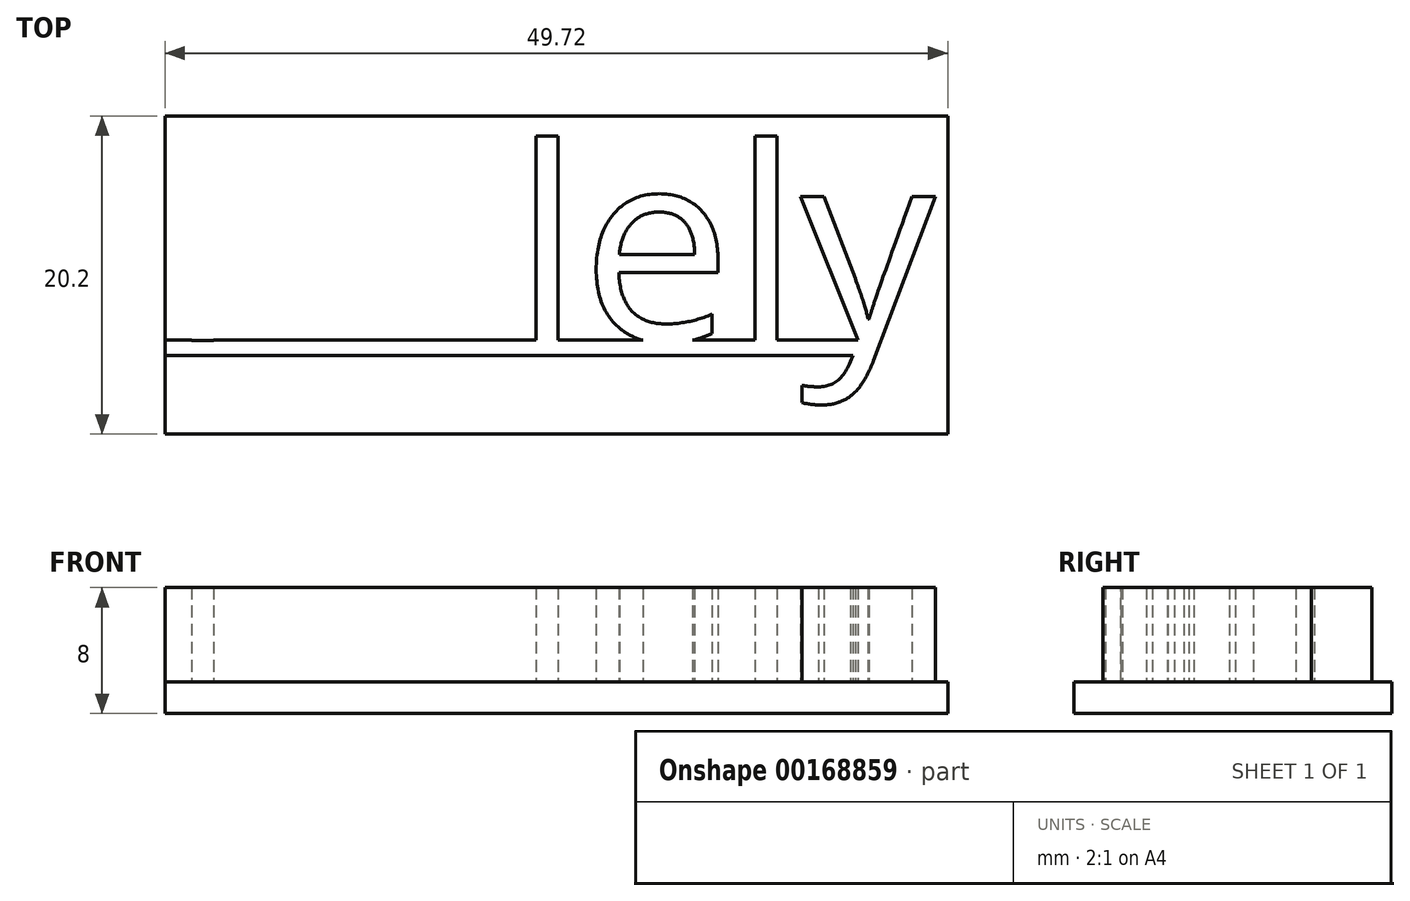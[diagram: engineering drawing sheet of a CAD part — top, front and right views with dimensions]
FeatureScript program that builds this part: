
annotation { "Feature Type Name" : "Feature", "Feature Type Description" : "" }
export const myFeature = defineFeature(function(context is Context, id is Id, definition is map)
    precondition{}
    {
        {
            var Q0;
            Q0=qCreatedBy(makeId("Top.planeOp"),FACE);
            var sketch = newSketch(context, id + "F0", { "sketchPlane" : qUnion([Q0])});
            skText(sketch, "E0", { "text": "Halely", "fontName": "OpenSans-Regular.ttf"});
            skLineSegment(sketch, "E1.bottom", {"start": v(0, -12.3) * mm, "end": v(50, -12.3) * mm});
            skLineSegment(sketch, "E1.top", {"start": v(0, -13.27) * mm, "end": v(50, -13.27) * mm});
            skLineSegment(sketch, "E1.left", {"start": v(0, -12.3) * mm, "end": v(0, -13.27) * mm});
            skLineSegment(sketch, "E1.right", {"start": v(50, -12.3) * mm, "end": v(50, -13.27) * mm});
            const initialGuessF0  = {"E0": [0, -0.0123, 1, 0, 0.0123]};
            skSetInitialGuess(sketch, initialGuessF0);
            skSolve(sketch);
        }
        {
            var Q0;
            {var subQ0=sQuery(id+"F0.wireOp",EDGE,"E0.sketch_text.stroke-1");Q0=makeQuery(id+"F0.imprint","IMPRINT",FACE,{"disambiguationData":[TD([[makeQuery(id+"F0.imprint","IMPRINT",EDGE,{"derivedFrom":subQ0}),-1.0]])]});}
            var Q1;
            {var subQ16=sQuery(id+"F0.wireOp",EDGE,"E0.sketch_text.stroke-56");Q1=makeQuery(id+"F0.imprint","IMPRINT",FACE,{"disambiguationData":[TD([[makeQuery(id+"F0.imprint","IMPRINT",EDGE,{"derivedFrom":subQ16}),1.0]])]});}
            var Q2;
            {var subQ5=sQuery(id+"F0.wireOp",EDGE,"E0.sketch_text.stroke-12");Q2=makeQuery(id+"F0.imprint","IMPRINT",FACE,{"disambiguationData":[TD([[makeQuery(id+"F0.imprint","IMPRINT",EDGE,{"derivedFrom":subQ5}),-1.0]])]});}
            var Q3;
            {var subQ0=sQuery(id+"F0.wireOp",EDGE,"E0.sketch_text.stroke-40");Q3=makeQuery(id+"F0.imprint","IMPRINT",FACE,{"disambiguationData":[TD([[makeQuery(id+"F0.imprint","IMPRINT",EDGE,{"derivedFrom":subQ0}),-1.0]])]});}
            var Q4;
            {var subQ0=sQuery(id+"F0.wireOp",EDGE,"E0.sketch_text.stroke-44");Q4=makeQuery(id+"F0.imprint","IMPRINT",FACE,{"disambiguationData":[TD([[makeQuery(id+"F0.imprint","IMPRINT",EDGE,{"derivedFrom":subQ0}),-1.0]])]});}
            var Q5;
            {var subQ0=sQuery(id+"F0.wireOp",EDGE,"E0.sketch_text.stroke-63");Q5=makeQuery(id+"F0.imprint","IMPRINT",FACE,{"disambiguationData":[TD([[makeQuery(id+"F0.imprint","IMPRINT",EDGE,{"derivedFrom":subQ0}),-1.0]])]});}
            var Q6;
            {var subQ0=sQuery(id+"F0.wireOp",EDGE,"E0.sketch_text.stroke-66");Q6=makeQuery(id+"F0.imprint","IMPRINT",FACE,{"disambiguationData":[TD([[makeQuery(id+"F0.imprint","IMPRINT",EDGE,{"derivedFrom":subQ0}),-1.0]])]});}
            var Q7;
            {var subQ0=sQuery(id+"F0.wireOp",EDGE,"E1.bottom");var subQ1=sQuery(id+"F0.wireOp",EDGE,"E0.sketch_text.stroke-73");var subQ2=makeQuery(id+"F0.imprint","INTERSECT",VERTEX,{"derivedFrom":[subQ1,subQ0]});Q7=makeQuery(id+"F0.imprint","IMPRINT",FACE,{"disambiguationData":[TD([[makeQuery(id+"F0.imprint","IMPRINT",EDGE,{"disambiguationData":[TD([[subQ2,-1.0]])],"derivedFrom":subQ1}),-1.0]])]});}
            var Q8;
            {var subQ5=sQuery(id+"F0.wireOp",EDGE,"E0.sketch_text.stroke-74");Q8=makeQuery(id+"F0.imprint","IMPRINT",FACE,{"disambiguationData":[TD([[makeQuery(id+"F0.imprint","IMPRINT",EDGE,{"derivedFrom":subQ5}),-1.0]])]});}
            var Q9;
            {var subQ0=sQuery(id+"F0.wireOp",EDGE,"E0.sketch_text.stroke-56");Q9=makeQuery(id+"F0.imprint","IMPRINT",FACE,{"disambiguationData":[TD([[makeQuery(id+"F0.imprint","IMPRINT",EDGE,{"derivedFrom":subQ0}),-1.0]])]});}
            var Q10;
            {var subQ0=sQuery(id+"F0.wireOp",EDGE,"E0.sketch_text.stroke-16");var subQ1=sQuery(id+"F0.wireOp",EDGE,"E0.sketch_text.stroke-15");var subQ2=makeQuery(id+"F0.imprint","INTERSECT",VERTEX,{"derivedFrom":[subQ1,subQ0]});Q10=makeQuery(id+"F0.imprint","IMPRINT",FACE,{"disambiguationData":[TD([[makeQuery(id+"F0.imprint","IMPRINT",EDGE,{"disambiguationData":[TD([[subQ2,1.0]])],"derivedFrom":subQ1}),-1.0]])]});}
            extrude(context, id + "F1", {"entities" : qUnion([Q0, Q1, Q2, Q3, Q4, Q5, Q6, Q7, Q8, Q9, Q10]), "depth" : 8 * mm});
        }
        {
            var Q0;
            Q0=qCreatedBy(makeId("Top.planeOp"),FACE);
            var sketch = newSketch(context, id + "F2", { "sketchPlane" : qUnion([Q0])});
            skLineSegment(sketch, "E2.bottom", {"start": v(49.72, -18.25) * mm, "end": v(0, -18.25) * mm});
            skLineSegment(sketch, "E2.top", {"start": v(49.72, 1.95) * mm, "end": v(0, 1.95) * mm});
            skLineSegment(sketch, "E2.left", {"start": v(49.72, -18.25) * mm, "end": v(49.72, 1.95) * mm});
            skLineSegment(sketch, "E2.right", {"start": v(0, -18.25) * mm, "end": v(0, 1.95) * mm});
            skSolve(sketch);
        }
        {
            var Q0;
            Q0 = qSketchRegion(id + "F2", true);
            extrude(context, id + "F3", {"entities" : qUnion([Q0]), "operationType" : NewBodyOperationType.ADD, "depth" : 2 * mm});
        }
    });
